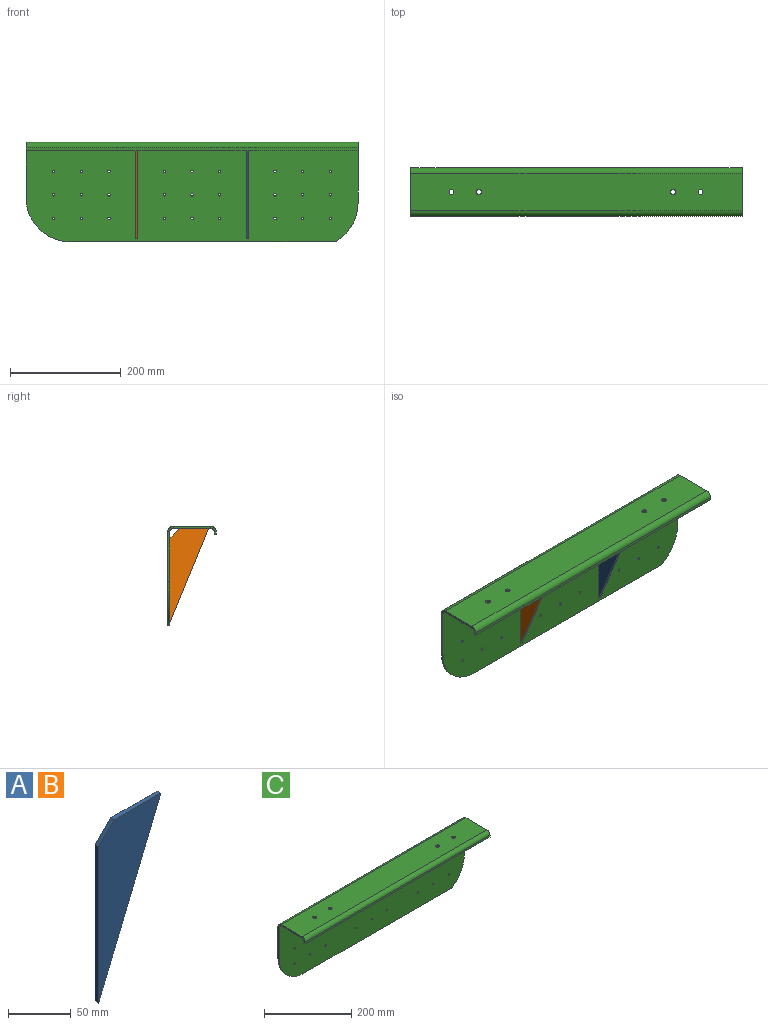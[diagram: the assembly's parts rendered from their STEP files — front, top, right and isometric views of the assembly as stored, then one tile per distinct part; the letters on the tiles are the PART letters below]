
ASSEMBLY  parts=3 mates=6
PART A: 6 faces, bbox 70x4x170 mm
  f0: plane 17.68x17.68mm, normal (-0.71,0,0.71), area 100mm2, adj f1,f3,f4,f5
  f1: plane 152.32x4mm, normal (-1,0,0), area 609.3mm2, adj f0,f2,f4,f5
  f2: plane 170x70mm, normal (0.92,0,-0.38), area 735.4mm2, adj f1,f3,f4,f5
  f3: plane 52.32x4mm, normal (0,0,1), area 209.3mm2, adj f0,f2,f4,f5
  f4: plane 170x70mm, normal (0,-1,0), area 5793.7mm2, adj f0,f1,f2,f3
  f5: plane 170x70mm, normal (0,1,0), area 5793.7mm2, adj f0,f1,f2,f3
PART B: same geometry as A
PART C: 55 faces, bbox 600x88x180 mm
  f0: plane 68x4mm, normal (-1,0,0), area 272mm2, adj f6,f7,f14,f51
  f1: cylinder r=4.5mm len=9mm, axis (0,0,1), area 113.1mm2, adj f6,f7
  f2: cylinder r=4.5mm len=9mm, axis (0,0,1), area 113.1mm2, adj f6,f7
  f3: cylinder r=4.5mm len=9mm, axis (0,0,1), area 113.1mm2, adj f6,f7
  f4: cylinder r=4.5mm len=9mm, axis (0,0,1), area 113.1mm2, adj f6,f7
  f5: plane 68x4mm, normal (1,0,0), area 272mm2, adj f6,f7,f13,f52
  f6: plane 600x68mm, normal (0,0,-1), area 40545.5mm2, adj f0,f1,f2,f3,f4,f5,f16,f54
  f7: plane 600x68mm, normal (0,0,1), area 40545.5mm2, adj f0,f1,f2,f3,f4,f5,f15,f53
  f8: plane 600x4mm, normal (0,0,-1), area 2400mm2, adj f9,f10,f11,f12
  f9: plane 5x4mm, normal (-1,0,0), area 20mm2, adj f8,f11,f12,f14
  f10: plane 5x4mm, normal (1,0,0), area 20mm2, adj f8,f11,f12,f13
  f11: plane 600x5mm, normal (0,1,0), area 3000mm2, adj f8,f9,f10,f16
  f12: plane 600x5mm, normal (0,-1,0), area 3000mm2, adj f8,f9,f10,f15
  f13: plane 10x10mm, normal (1,0,0), area 50.3mm2, adj f5,f10,f15,f16
  f14: plane 10x10mm, normal (-1,0,0), area 50.3mm2, adj f0,f9,f15,f16
  f15: cylinder r=10mm len=600mm, axis (1,0,0), area 9424.8mm2, adj f7,f12,f13,f14
  f16: cylinder r=6mm len=600mm, axis (1,0,0), area 5654.9mm2, adj f6,f11,f13,f14
  f17: cylinder r=80mm len=70mm, axis (0,-1,0), area 340.9mm2, adj f18,f48,f49,f50
  f18: plane 100x4mm, normal (1,0,0), area 400mm2, adj f17,f49,f50,f52
  f19: plane 90x4mm, normal (-1,0,0), area 360mm2, adj f20,f49,f50,f51
  f20: cylinder r=80mm len=80mm, axis (0,-1,0), area 502.7mm2, adj f19,f48,f49,f50
  f21: cylinder r=2.25mm len=4.5mm, axis (0,-1,0), area 56.5mm2, adj f49,f50
  f22: cylinder r=2.25mm len=4.5mm, axis (0,-1,0), area 56.5mm2, adj f49,f50
  f23: cylinder r=2.25mm len=4.5mm, axis (0,-1,0), area 56.5mm2, adj f49,f50
  f24: cylinder r=2.25mm len=4.5mm, axis (0,-1,0), area 56.5mm2, adj f49,f50
  f25: cylinder r=2.25mm len=4.5mm, axis (0,-1,0), area 56.5mm2, adj f49,f50
  f26: cylinder r=2.25mm len=4.5mm, axis (0,-1,0), area 56.5mm2, adj f49,f50
  f27: cylinder r=2.25mm len=4.5mm, axis (0,-1,0), area 56.5mm2, adj f49,f50
  f28: cylinder r=2.25mm len=4.5mm, axis (0,-1,0), area 56.5mm2, adj f49,f50
  f29: cylinder r=2.25mm len=4.5mm, axis (0,-1,0), area 56.5mm2, adj f49,f50
  f30: cylinder r=2.25mm len=4.5mm, axis (0,-1,0), area 56.5mm2, adj f49,f50
  f31: cylinder r=2.25mm len=4.5mm, axis (0,-1,0), area 56.5mm2, adj f49,f50
  f32: cylinder r=2.25mm len=4.5mm, axis (0,-1,0), area 56.5mm2, adj f49,f50
  f33: cylinder r=2.25mm len=4.5mm, axis (0,-1,0), area 56.5mm2, adj f49,f50
  f34: cylinder r=2.25mm len=4.5mm, axis (0,-1,0), area 56.5mm2, adj f49,f50
  f35: cylinder r=2.25mm len=4.5mm, axis (0,-1,0), area 56.5mm2, adj f49,f50
  f36: cylinder r=2.25mm len=4.5mm, axis (0,-1,0), area 56.5mm2, adj f49,f50
  f37: cylinder r=2.25mm len=4.5mm, axis (0,-1,0), area 56.5mm2, adj f49,f50
  f38: cylinder r=2.25mm len=4.5mm, axis (0,-1,0), area 56.5mm2, adj f49,f50
  f39: cylinder r=2.25mm len=4.5mm, axis (0,-1,0), area 56.5mm2, adj f49,f50
  f40: cylinder r=2.25mm len=4.5mm, axis (0,-1,0), area 56.5mm2, adj f49,f50
  f41: cylinder r=2.25mm len=4.5mm, axis (0,-1,0), area 56.5mm2, adj f49,f50
  f42: cylinder r=2.25mm len=4.5mm, axis (0,-1,0), area 56.5mm2, adj f49,f50
  f43: cylinder r=2.25mm len=4.5mm, axis (0,-1,0), area 56.5mm2, adj f49,f50
  f44: cylinder r=2.25mm len=4.5mm, axis (0,-1,0), area 56.5mm2, adj f49,f50
  f45: cylinder r=2.25mm len=4.5mm, axis (0,-1,0), area 56.5mm2, adj f49,f50
  f46: cylinder r=2.25mm len=4.5mm, axis (0,-1,0), area 56.5mm2, adj f49,f50
  f47: cylinder r=2.25mm len=4.5mm, axis (0,-1,0), area 56.5mm2, adj f49,f50
  f48: plane 478.73x4mm, normal (0,0,-1), area 1914.9mm2, adj f17,f20,f49,f50
  f49: plane 600x170mm, normal (0,-1,0), area 99362.1mm2, adj f17,f18,f19,f20,f21,f22,f23,f24
  f50: plane 600x170mm, normal (0,1,0), area 99362.1mm2, adj f17,f18,f19,f20,f21,f22,f23,f24
  f51: plane 10x10mm, normal (-1,0,0), area 50.3mm2, adj f0,f19,f53,f54
  f52: plane 10x10mm, normal (1,0,0), area 50.3mm2, adj f5,f18,f53,f54
  f53: cylinder r=10mm len=600mm, axis (-1,0,0), area 9424.8mm2, adj f7,f50,f51,f52
  f54: cylinder r=6mm len=600mm, axis (-1,0,0), area 5654.9mm2, adj f6,f49,f51,f52
PLACE A rot(axis=(0,0,-1),90deg) t=(402,0,-20)mm
PLACE B rot(axis=(0,0,-1),90deg) t=(202,0,-20)mm
PLACE C at identity fixed
MATE parallel A.f5 <-> C.f18  axis (1,0,0) through (402,-23.8,-58.04)mm
MATE planar C.f6 <-> B.f3  axis (0,0,-1) through (300,-40,0)mm
MATE planar A.f3 <-> C.f6  axis (0,0,1) through (400,-43.84,0)mm
MATE planar A.f1 <-> C.f49  axis (0,1,0) through (400,0,-93.84)mm
MATE planar B.f1 <-> C.f49  axis (0,1,0) through (200,0,-93.84)mm
MATE parallel B.f5 <-> A.f5  axis (1,0,0) through (202,-23.8,-58.04)mm
